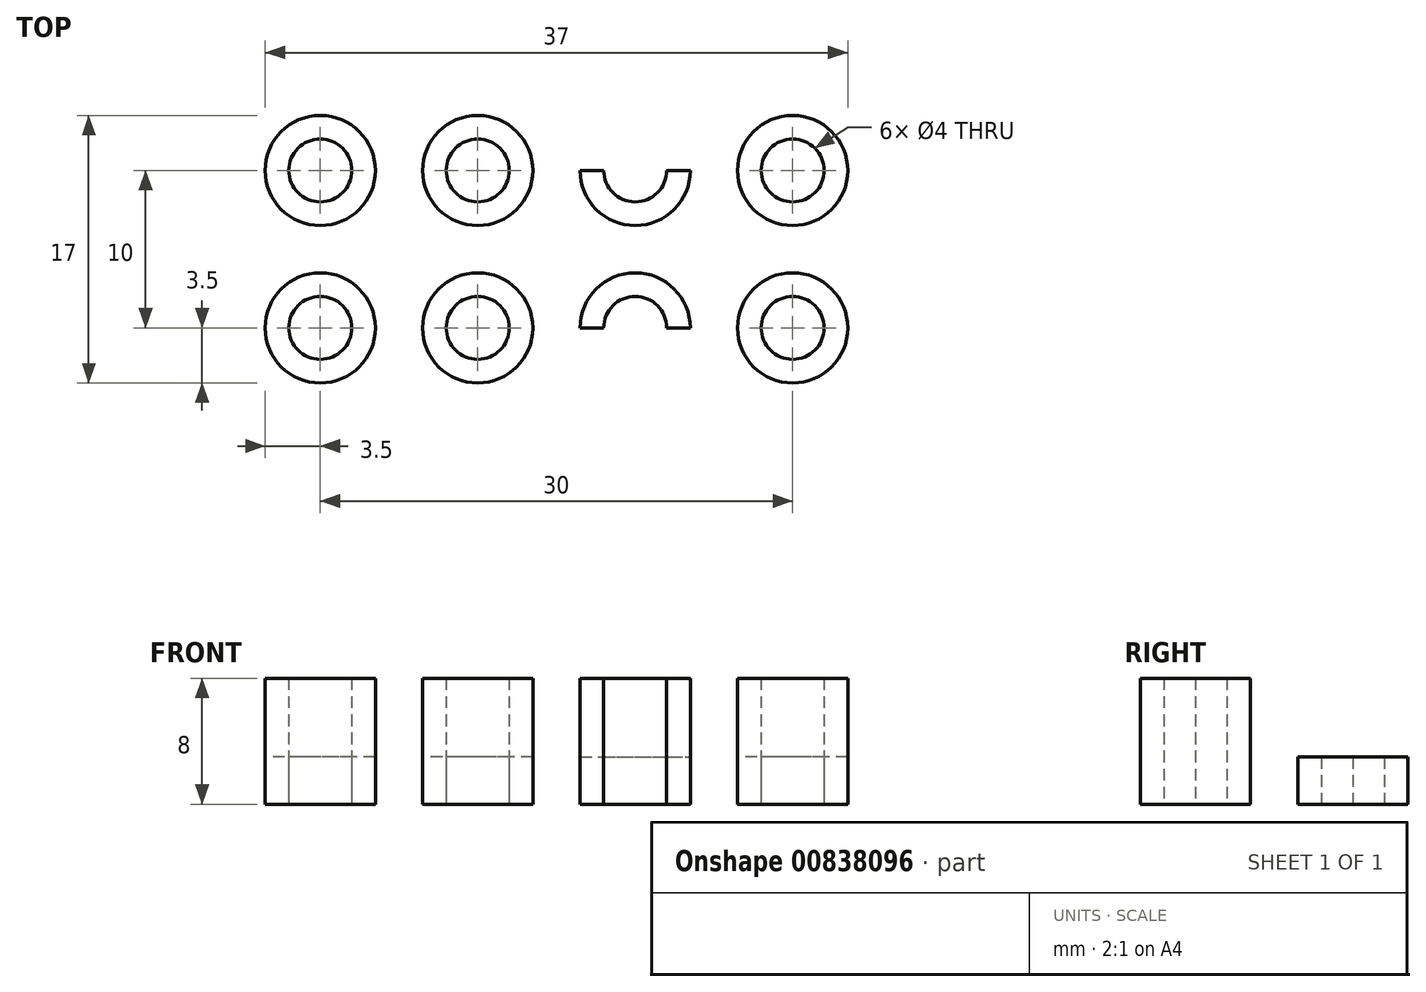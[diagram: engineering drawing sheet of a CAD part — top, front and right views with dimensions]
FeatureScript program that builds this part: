
annotation { "Feature Type Name" : "Feature", "Feature Type Description" : "" }
export const myFeature = defineFeature(function(context is Context, id is Id, definition is map)
    precondition{}
    {
        {
            var Q0;
            Q0=qCreatedBy(makeId("Top.planeOp"),FACE);
            var sketch = newSketch(context, id + "F0", { "sketchPlane" : qUnion([Q0])});
            skLineSegment(sketch, "E0.bottom", {"start": v(-5, -5) * mm, "end": v(5, -5) * mm});
            skLineSegment(sketch, "E0.top", {"start": v(-5, 5) * mm, "end": v(5, 5) * mm});
            skLineSegment(sketch, "E0.left", {"start": v(-5, -5) * mm, "end": v(-5, 5) * mm});
            skLineSegment(sketch, "E0.right", {"start": v(5, -5) * mm, "end": v(5, 5) * mm});
            skLineSegment(sketch, "E1.bottom", {"start": v(-15, 5) * mm, "end": v(15, 5) * mm});
            skLineSegment(sketch, "E1.top", {"start": v(-15, -5) * mm, "end": v(15, -5) * mm});
            skLineSegment(sketch, "E1.left", {"start": v(-15, 5) * mm, "end": v(-15, -5) * mm});
            skLineSegment(sketch, "E1.right", {"start": v(15, 5) * mm, "end": v(15, -5) * mm});
            skCircle(sketch, "E2", {"center": v(-15, 5) * mm, "radius": 2 * mm});
            skCircle(sketch, "E3", {"center": v(-15, 5) * mm, "radius": 3.5 * mm});
            skCircle(sketch, "E4", {"center": v(-5, 5) * mm, "radius": 2 * mm});
            skCircle(sketch, "E5", {"center": v(-5, 5) * mm, "radius": 3.5 * mm});
            skCircle(sketch, "E6", {"center": v(5, 5) * mm, "radius": 2 * mm});
            skCircle(sketch, "E7", {"center": v(5, 5) * mm, "radius": 3.5 * mm});
            skCircle(sketch, "E8", {"center": v(15, 5) * mm, "radius": 2 * mm});
            skCircle(sketch, "E9", {"center": v(15, 5) * mm, "radius": 3.5 * mm});
            skCircle(sketch, "E10", {"center": v(-15, -5) * mm, "radius": 2 * mm});
            skCircle(sketch, "E11", {"center": v(-15, -5) * mm, "radius": 3.5 * mm});
            skCircle(sketch, "E12", {"center": v(-5, -5) * mm, "radius": 2 * mm});
            skCircle(sketch, "E13", {"center": v(-5, -5) * mm, "radius": 3.5 * mm});
            skCircle(sketch, "E14", {"center": v(5, -5) * mm, "radius": 2 * mm});
            skCircle(sketch, "E15", {"center": v(5, -5) * mm, "radius": 3.5 * mm});
            skCircle(sketch, "E16", {"center": v(15, -5) * mm, "radius": 2 * mm});
            skCircle(sketch, "E17", {"center": v(15, -5) * mm, "radius": 3.5 * mm});
            skSolve(sketch);
        }
        {
            var Q0;
            {var subQ0=sQuery(id+"F0.wireOp",EDGE,"E3");var subQ1=sQuery(id+"F0.wireOp",EDGE,"E1.bottom");var subQ2=makeQuery(id+"F0.imprint","INTERSECT",VERTEX,{"derivedFrom":[subQ1,subQ0]});Q0=makeQuery(id+"F0.imprint","IMPRINT",FACE,{"disambiguationData":[TD([[makeQuery(id+"F0.imprint","IMPRINT",EDGE,{"disambiguationData":[TD([[subQ2,1.0]])],"derivedFrom":subQ1}),1.0]])]});}
            var Q1;
            {var subQ0=sQuery(id+"F0.wireOp",EDGE,"E3");var subQ1=sQuery(id+"F0.wireOp",EDGE,"E1.bottom");var subQ2=makeQuery(id+"F0.imprint","INTERSECT",VERTEX,{"derivedFrom":[subQ1,subQ0]});Q1=makeQuery(id+"F0.imprint","IMPRINT",FACE,{"disambiguationData":[TD([[makeQuery(id+"F0.imprint","IMPRINT",EDGE,{"disambiguationData":[TD([[subQ2,1.0]])],"derivedFrom":subQ1}),-1.0]])]});}
            var Q2;
            {var subQ0=sQuery(id+"F0.wireOp",EDGE,"E5");var subQ1=sQuery(id+"F0.wireOp",EDGE,"E1.bottom");var subQ2=makeQuery(id+"F0.imprint","INTERSECT",VERTEX,{"disambiguationData":[OD(0.0)],"derivedFrom":[subQ1,subQ0]});Q2=makeQuery(id+"F0.imprint","IMPRINT",FACE,{"disambiguationData":[TD([[makeQuery(id+"F0.imprint","IMPRINT",EDGE,{"disambiguationData":[TD([[subQ2,-1.0]])],"derivedFrom":subQ1}),1.0]])]});}
            var Q3;
            {var subQ0=sQuery(id+"F0.wireOp",EDGE,"E5");var subQ1=sQuery(id+"F0.wireOp",EDGE,"E0.left");var subQ2=makeQuery(id+"F0.imprint","INTERSECT",VERTEX,{"derivedFrom":[subQ1,subQ0]});Q3=makeQuery(id+"F0.imprint","IMPRINT",FACE,{"disambiguationData":[TD([[makeQuery(id+"F0.imprint","IMPRINT",EDGE,{"disambiguationData":[TD([[subQ2,-1.0]])],"derivedFrom":subQ1}),-1.0]])]});}
            var Q4;
            {var subQ0=sQuery(id+"F0.wireOp",EDGE,"E5");var subQ1=sQuery(id+"F0.wireOp",EDGE,"E0.left");var subQ2=makeQuery(id+"F0.imprint","INTERSECT",VERTEX,{"derivedFrom":[subQ1,subQ0]});Q4=makeQuery(id+"F0.imprint","IMPRINT",FACE,{"disambiguationData":[TD([[makeQuery(id+"F0.imprint","IMPRINT",EDGE,{"disambiguationData":[TD([[subQ2,-1.0]])],"derivedFrom":subQ1}),1.0]])]});}
            var Q5;
            {var subQ0=sQuery(id+"F0.wireOp",EDGE,"E7");var subQ1=sQuery(id+"F0.wireOp",EDGE,"E0.right");var subQ2=makeQuery(id+"F0.imprint","INTERSECT",VERTEX,{"derivedFrom":[subQ1,subQ0]});Q5=makeQuery(id+"F0.imprint","IMPRINT",FACE,{"disambiguationData":[TD([[makeQuery(id+"F0.imprint","IMPRINT",EDGE,{"disambiguationData":[TD([[subQ2,-1.0]])],"derivedFrom":subQ1}),1.0]])]});}
            var Q6;
            {var subQ0=sQuery(id+"F0.wireOp",EDGE,"E7");var subQ1=sQuery(id+"F0.wireOp",EDGE,"E0.right");var subQ2=makeQuery(id+"F0.imprint","INTERSECT",VERTEX,{"derivedFrom":[subQ1,subQ0]});Q6=makeQuery(id+"F0.imprint","IMPRINT",FACE,{"disambiguationData":[TD([[makeQuery(id+"F0.imprint","IMPRINT",EDGE,{"disambiguationData":[TD([[subQ2,-1.0]])],"derivedFrom":subQ1}),-1.0]])]});}
            var Q7;
            {var subQ0=sQuery(id+"F0.wireOp",EDGE,"E7");var subQ1=sQuery(id+"F0.wireOp",EDGE,"E1.bottom");var subQ2=makeQuery(id+"F0.imprint","INTERSECT",VERTEX,{"disambiguationData":[OD(0.0)],"derivedFrom":[subQ1,subQ0]});Q7=makeQuery(id+"F0.imprint","IMPRINT",FACE,{"disambiguationData":[TD([[makeQuery(id+"F0.imprint","IMPRINT",EDGE,{"disambiguationData":[TD([[subQ2,-1.0]])],"derivedFrom":subQ1}),1.0]])]});}
            var Q8;
            {var subQ0=sQuery(id+"F0.wireOp",EDGE,"E9");var subQ1=sQuery(id+"F0.wireOp",EDGE,"E1.bottom");var subQ2=makeQuery(id+"F0.imprint","INTERSECT",VERTEX,{"derivedFrom":[subQ1,subQ0]});Q8=makeQuery(id+"F0.imprint","IMPRINT",FACE,{"disambiguationData":[TD([[makeQuery(id+"F0.imprint","IMPRINT",EDGE,{"disambiguationData":[TD([[subQ2,-1.0]])],"derivedFrom":subQ1}),1.0]])]});}
            var Q9;
            {var subQ0=sQuery(id+"F0.wireOp",EDGE,"E9");var subQ1=sQuery(id+"F0.wireOp",EDGE,"E1.bottom");var subQ2=makeQuery(id+"F0.imprint","INTERSECT",VERTEX,{"derivedFrom":[subQ1,subQ0]});Q9=makeQuery(id+"F0.imprint","IMPRINT",FACE,{"disambiguationData":[TD([[makeQuery(id+"F0.imprint","IMPRINT",EDGE,{"disambiguationData":[TD([[subQ2,-1.0]])],"derivedFrom":subQ1}),-1.0]])]});}
            extrude(context, id + "F1", {"entities" : qUnion([Q0, Q1, Q2, Q3, Q4, Q5, Q6, Q7, Q8, Q9]), "depth" : 3 * mm, "offsetDistance" : 25 * mm});
        }
        {
            var Q0;
            {var subQ0=sQuery(id+"F0.wireOp",EDGE,"E11");var subQ1=sQuery(id+"F0.wireOp",EDGE,"E1.top");var subQ2=makeQuery(id+"F0.imprint","INTERSECT",VERTEX,{"derivedFrom":[subQ1,subQ0]});Q0=makeQuery(id+"F0.imprint","IMPRINT",FACE,{"disambiguationData":[TD([[makeQuery(id+"F0.imprint","IMPRINT",EDGE,{"disambiguationData":[TD([[subQ2,1.0]])],"derivedFrom":subQ1}),-1.0]])]});}
            var Q1;
            {var subQ0=sQuery(id+"F0.wireOp",EDGE,"E11");var subQ1=sQuery(id+"F0.wireOp",EDGE,"E1.top");var subQ2=makeQuery(id+"F0.imprint","INTERSECT",VERTEX,{"derivedFrom":[subQ1,subQ0]});Q1=makeQuery(id+"F0.imprint","IMPRINT",FACE,{"disambiguationData":[TD([[makeQuery(id+"F0.imprint","IMPRINT",EDGE,{"disambiguationData":[TD([[subQ2,1.0]])],"derivedFrom":subQ1}),1.0]])]});}
            var Q2;
            {var subQ0=sQuery(id+"F0.wireOp",EDGE,"E12");var subQ1=sQuery(id+"F0.wireOp",EDGE,"E0.left");var subQ2=makeQuery(id+"F0.imprint","INTERSECT",VERTEX,{"derivedFrom":[subQ1,subQ0]});Q2=makeQuery(id+"F0.imprint","IMPRINT",FACE,{"disambiguationData":[TD([[makeQuery(id+"F0.imprint","IMPRINT",EDGE,{"disambiguationData":[TD([[subQ2,-1.0]])],"derivedFrom":subQ1}),1.0]])]});}
            var Q3;
            {var subQ0=sQuery(id+"F0.wireOp",EDGE,"E12");var subQ1=sQuery(id+"F0.wireOp",EDGE,"E0.left");var subQ2=makeQuery(id+"F0.imprint","INTERSECT",VERTEX,{"derivedFrom":[subQ1,subQ0]});Q3=makeQuery(id+"F0.imprint","IMPRINT",FACE,{"disambiguationData":[TD([[makeQuery(id+"F0.imprint","IMPRINT",EDGE,{"disambiguationData":[TD([[subQ2,-1.0]])],"derivedFrom":subQ1}),-1.0]])]});}
            var Q4;
            {var subQ0=sQuery(id+"F0.wireOp",EDGE,"E13");var subQ1=sQuery(id+"F0.wireOp",EDGE,"E1.top");var subQ2=makeQuery(id+"F0.imprint","INTERSECT",VERTEX,{"disambiguationData":[OD(0.0)],"derivedFrom":[subQ1,subQ0]});Q4=makeQuery(id+"F0.imprint","IMPRINT",FACE,{"disambiguationData":[TD([[makeQuery(id+"F0.imprint","IMPRINT",EDGE,{"disambiguationData":[TD([[subQ2,-1.0]])],"derivedFrom":subQ1}),-1.0]])]});}
            var Q5;
            {var subQ0=sQuery(id+"F0.wireOp",EDGE,"E14");var subQ1=sQuery(id+"F0.wireOp",EDGE,"E0.right");var subQ2=makeQuery(id+"F0.imprint","INTERSECT",VERTEX,{"derivedFrom":[subQ1,subQ0]});Q5=makeQuery(id+"F0.imprint","IMPRINT",FACE,{"disambiguationData":[TD([[makeQuery(id+"F0.imprint","IMPRINT",EDGE,{"disambiguationData":[TD([[subQ2,-1.0]])],"derivedFrom":subQ1}),1.0]])]});}
            var Q6;
            {var subQ0=sQuery(id+"F0.wireOp",EDGE,"E15");var subQ1=sQuery(id+"F0.wireOp",EDGE,"E1.top");var subQ2=makeQuery(id+"F0.imprint","INTERSECT",VERTEX,{"disambiguationData":[OD(0.0)],"derivedFrom":[subQ1,subQ0]});Q6=makeQuery(id+"F0.imprint","IMPRINT",FACE,{"disambiguationData":[TD([[makeQuery(id+"F0.imprint","IMPRINT",EDGE,{"disambiguationData":[TD([[subQ2,-1.0]])],"derivedFrom":subQ1}),-1.0]])]});}
            var Q7;
            {var subQ0=sQuery(id+"F0.wireOp",EDGE,"E14");var subQ1=sQuery(id+"F0.wireOp",EDGE,"E0.right");var subQ2=makeQuery(id+"F0.imprint","INTERSECT",VERTEX,{"derivedFrom":[subQ1,subQ0]});Q7=makeQuery(id+"F0.imprint","IMPRINT",FACE,{"disambiguationData":[TD([[makeQuery(id+"F0.imprint","IMPRINT",EDGE,{"disambiguationData":[TD([[subQ2,-1.0]])],"derivedFrom":subQ1}),-1.0]])]});}
            var Q8;
            {var subQ0=sQuery(id+"F0.wireOp",EDGE,"E17");var subQ1=sQuery(id+"F0.wireOp",EDGE,"E1.top");var subQ2=makeQuery(id+"F0.imprint","INTERSECT",VERTEX,{"derivedFrom":[subQ1,subQ0]});Q8=makeQuery(id+"F0.imprint","IMPRINT",FACE,{"disambiguationData":[TD([[makeQuery(id+"F0.imprint","IMPRINT",EDGE,{"disambiguationData":[TD([[subQ2,-1.0]])],"derivedFrom":subQ1}),1.0]])]});}
            var Q9;
            {var subQ0=sQuery(id+"F0.wireOp",EDGE,"E17");var subQ1=sQuery(id+"F0.wireOp",EDGE,"E1.top");var subQ2=makeQuery(id+"F0.imprint","INTERSECT",VERTEX,{"derivedFrom":[subQ1,subQ0]});Q9=makeQuery(id+"F0.imprint","IMPRINT",FACE,{"disambiguationData":[TD([[makeQuery(id+"F0.imprint","IMPRINT",EDGE,{"disambiguationData":[TD([[subQ2,-1.0]])],"derivedFrom":subQ1}),-1.0]])]});}
            extrude(context, id + "F2", {"entities" : qUnion([Q0, Q1, Q2, Q3, Q4, Q5, Q6, Q7, Q8, Q9]), "depth" : 8 * mm, "offsetDistance" : 25 * mm});
        }
    });
